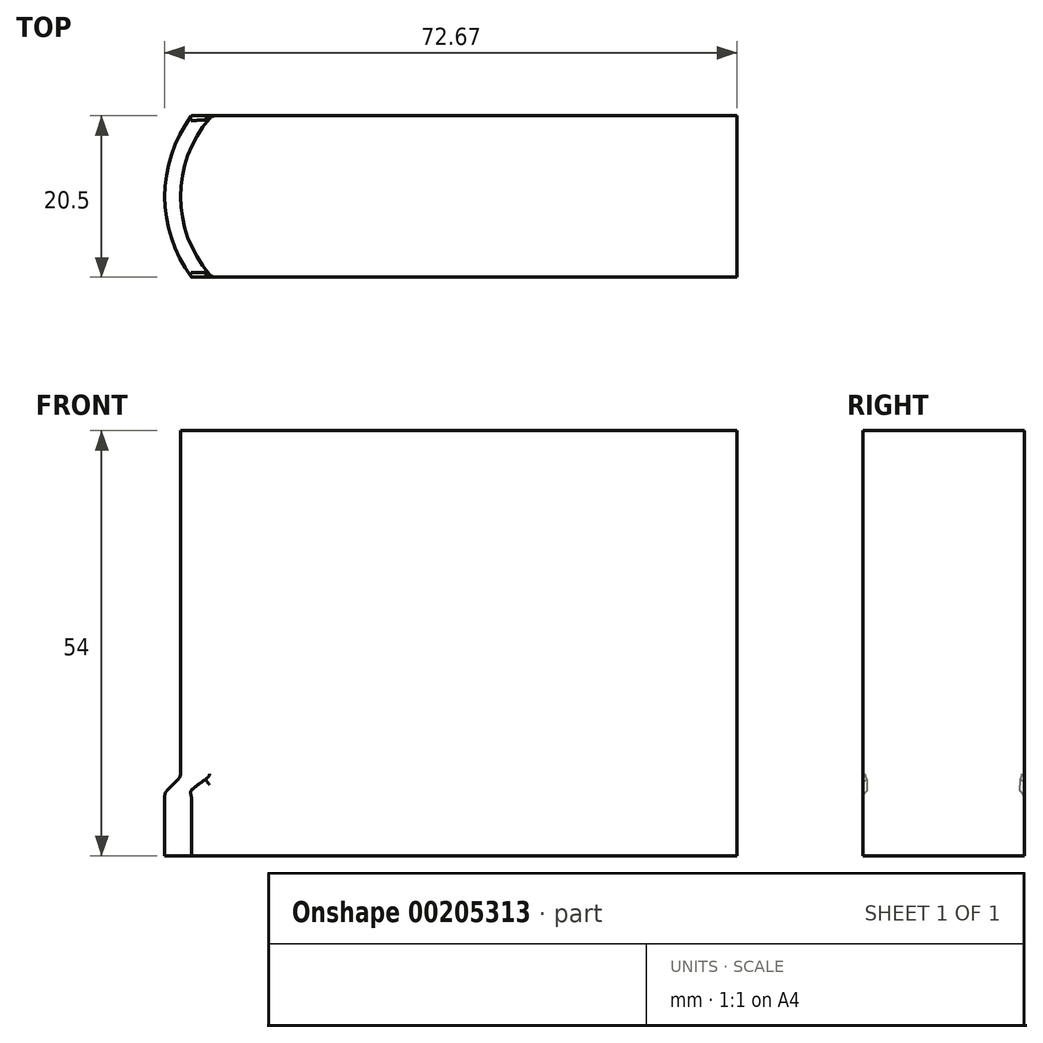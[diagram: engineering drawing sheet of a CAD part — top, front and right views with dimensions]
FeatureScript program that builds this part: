
annotation { "Feature Type Name" : "Feature", "Feature Type Description" : "" }
export const myFeature = defineFeature(function(context is Context, id is Id, definition is map)
    precondition{}
    {
        {
            var Q0;
            Q0=qCreatedBy(makeId("Top.planeOp"),FACE);
            var sketch = newSketch(context, id + "F0", { "sketchPlane" : qUnion([Q0])});
            skLineSegment(sketch, "E0.bottom", {"start": v(0, 0) * mm, "end": v(66.67, 0) * mm});
            skLineSegment(sketch, "E0.top", {"start": v(0, 20.5) * mm, "end": v(66.67, 20.5) * mm});
            skLineSegment(sketch, "E0.left", {"start": v(0, 0) * mm, "end": v(0, 20.5) * mm, "construction": true});
            skLineSegment(sketch, "E0.right", {"start": v(66.67, 0) * mm, "end": v(66.67, 20.5) * mm});
            skArc(sketch, "E1", {"start": v(0, 20.5) * mm, "mid": v(-4, 10.25) * mm, "end": v(0, 0) * mm});
            skSolve(sketch);
        }
        {
            var Q0;
            Q0=makeQuery(id+"F0.imprint","IMPRINT",FACE,{"disambiguationData":[TD([[makeQuery(id+"F0.imprint","IMPRINT",EDGE,{"derivedFrom":sQuery(id+"F0.wireOp",EDGE,"E0.bottom")}),1.0]])]});
            extrude(context, id + "F1", {"entities" : qUnion([Q0]), "depth" : 44 * mm});
        }
        {
            var Q0;
            Q0=makeQuery(id+"F1.opExtrude","CAP_FACE",FACE,{"disambiguationData":[OSD([sQuery(id+"F0.wireOp",EDGE,"E0.bottom"),sQuery(id+"F0.wireOp",EDGE,"E0.top"),sQuery(id+"F0.wireOp",EDGE,"E0.right"),sQuery(id+"F0.wireOp",EDGE,"E1")])],"isStart":true});
            var sketch = newSketch(context, id + "F2", { "sketchPlane" : qUnion([Q0])});
            skArc(sketch, "E2.0.0", {"start": v(0, 0) * mm, "mid": v(-4, -10.25) * mm, "end": v(0, -20.5) * mm});
            skLineSegment(sketch, "E2.0.1", {"start": v(0, -20.5) * mm, "end": v(66.67, -20.5) * mm});
            skLineSegment(sketch, "E2.0.2", {"start": v(66.67, -20.5) * mm, "end": v(66.67, 0) * mm});
            skLineSegment(sketch, "E2.0.3", {"start": v(66.67, 0) * mm, "end": v(0, 0) * mm});
            skArc(sketch, "E3.0", {"start": v(-2.6, 0) * mm, "mid": v(-6, -10.25) * mm, "end": v(-2.6, -20.5) * mm});
            skLineSegment(sketch, "E4", {"start": v(0, 0) * mm, "end": v(-2.6, 0) * mm});
            skLineSegment(sketch, "E5", {"start": v(0, -20.5) * mm, "end": v(-2.6, -20.5) * mm});
            skSolve(sketch);
        }
        {
            var Q0;
            Q0=makeQuery(id+"F2.imprint","IMPRINT",FACE,{"disambiguationData":[TD([[makeQuery(id+"F2.imprint","IMPRINT",EDGE,{"derivedFrom":sQuery(id+"F2.wireOp",EDGE,"E2.0.0")}),1.0]])]});
            var Q1;
            Q1=makeQuery(id+"F2.imprint","IMPRINT",FACE,{"disambiguationData":[TD([[makeQuery(id+"F2.imprint","IMPRINT",EDGE,{"derivedFrom":sQuery(id+"F2.wireOp",EDGE,"E2.0.0")}),-1.0]])]});
            extrude(context, id + "F3", {"entities" : qUnion([Q0, Q1]), "operationType" : NewBodyOperationType.ADD, "depth" : 10 * mm});
        }
        {
            var Q0;
            Q0=makeQuery(id+"F3.opExtrude","CAP_EDGE",EDGE,{"disambiguationData":[OSD([sQuery(id+"F2.wireOp",EDGE,"E3.0")])],"isStart":true});
            chamfer(context, id + "F4", {"entities" : qUnion([Q0]), "width" : 2 * mm, "tangentPropagation" : true});
        }
        {
            var Q0;
            Q0=makeQuery(id+"F4.opChamfer","BLEND_EDGE",EDGE,{"blendedFrom":[makeQuery(id+"F3.opExtrude","CAP_EDGE",EDGE,{"disambiguationData":[OSD([sQuery(id+"F2.wireOp",EDGE,"E3.0")])],"isStart":true}),makeQuery(id+"F1.opExtrude","SWEPT_FACE",FACE,{"disambiguationData":[OSD([sQuery(id+"F0.wireOp",EDGE,"E1")])]})],"blendedInto":[makeQuery(id+"F1.opExtrude","SWEPT_FACE",FACE,{"disambiguationData":[OSD([sQuery(id+"F0.wireOp",EDGE,"E1")])]})]});
            fillet(context, id + "F5", {"entities" : qUnion([Q0]), "radius" : 1 * mm, "tangentPropagation" : true, "allowEdgeOverflow" : false});
        }
        {
            var Q0;
            Q0=makeQuery(id+"F1.opExtrude","SWEPT_EDGE",EDGE,{"disambiguationData":[OSD([sQuery(id+"F0.wireOp",EDGE,"E0.bottom"),sQuery(id+"F0.wireOp",EDGE,"E1")])]});
            var Q1;
            Q1=makeQuery(id+"F1.opExtrude","SWEPT_EDGE",EDGE,{"disambiguationData":[OSD([sQuery(id+"F0.wireOp",EDGE,"E0.top"),sQuery(id+"F0.wireOp",EDGE,"E1")])]});
            var Q2;
            {var subQ0=sQuery(id+"F2.wireOp",EDGE,"E3.0");Q2=makeQuery(id+"F4.opChamfer","BLEND_EDGE",EDGE,{"blendedFrom":[makeQuery(id+"F3.opExtrude","CAP_EDGE",EDGE,{"disambiguationData":[OSD([subQ0])],"isStart":true}),makeQuery(id+"F3.opExtrude","SWEPT_FACE",FACE,{"disambiguationData":[OSD([subQ0])]})],"blendedInto":[makeQuery(id+"F3.opExtrude","SWEPT_FACE",FACE,{"disambiguationData":[OSD([subQ0])]})]});}
            fillet(context, id + "F6", {"entities" : qUnion([Q0, Q1, Q2]), "radius" : 1 * mm, "tangentPropagation" : true, "allowEdgeOverflow" : false});
        }
    });
